# Revit family: Medicine_Cabinet-Bradley_Corp-9663
name_source: partatom
category: Specialty Equipment
revit_build: Autodesk Revit MEP 2012 (Build: 20110309_2315(x64)
units: mm (PartAtom-declared; Revit-internal decimal feet)

## types (1)
- Medicine_Cabinet-Bradley_Corp-9663
    ADA Compliant = No
    Assembly Code = C1030200
    Buy American Act = To Be Determined
    Default Elevation = 5' - 0"
    Description = Medicine Cabinet
    Door Material = Metal - Bradley Corp - Steel
    Height = 2' - 2"
    Length = 0' - 4 1/2"
    Low Emitting Material = No
    Manufacturer = Bradley Corporation
    MasterFormat Number = 10.28.13.19
    MasterFormat Title = Toilet, Bath, and Laundry Accessories
    Material = Steel
    Model = 9663
    OmniClass Table 21 Number = 21-03 10 90 40
    OmniClass Table 21 Title = Toilet, Bath, and Laundry Accessories
    OmniClass Table 23 Number = 23.25.53.11.13.11
    OmniClass Table 23 Title = Medicine Cabinets
    Percentage of Recycled Content = 0
    Product Tech Data URL - English = http://bradleycorp.com
    Shelf Material = Metal - Bradley Corp - Steel
    Specifications URL = http://www.bradleycorp.com
    URL = http://www.bradleycorp.com
    Version = 2.0
    Warranty Information = Complete Unit, One Year
    Width = 1' - 4"

## geometry (parser evidence)
native form markers: Blend x2, Sweep x3
no freeform markers — native parametric forms only
